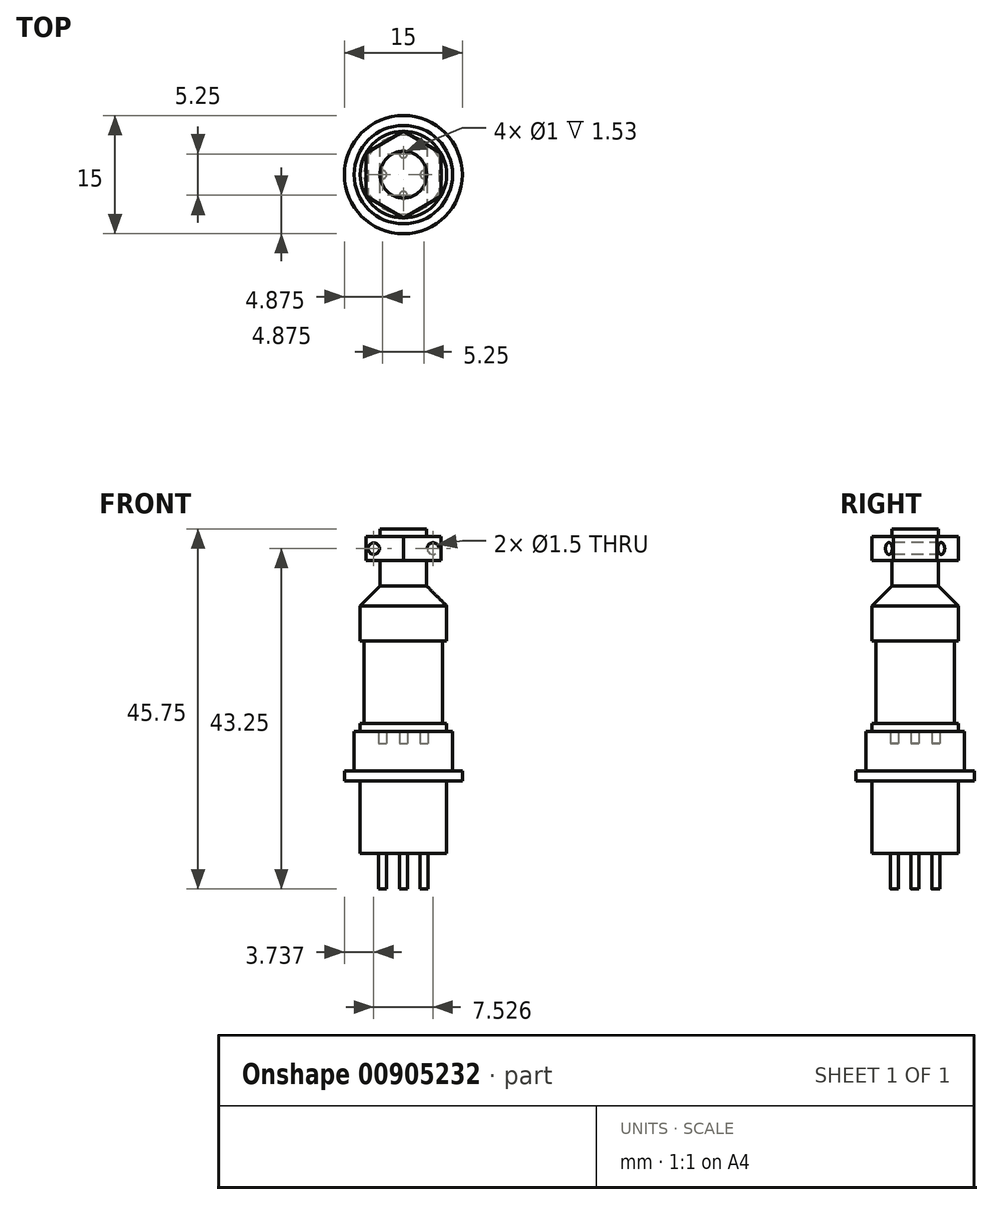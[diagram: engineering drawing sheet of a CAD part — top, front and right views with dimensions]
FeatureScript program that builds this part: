
annotation { "Feature Type Name" : "Feature", "Feature Type Description" : "" }
export const myFeature = defineFeature(function(context is Context, id is Id, definition is map)
    precondition{}
    {
        {
            var Q0;
            Q0=qCreatedBy(makeId("Top.planeOp"),FACE);
            var sketch = newSketch(context, id + "F0", { "sketchPlane" : qUnion([Q0])});
            skCircle(sketch, "E0", {"center": v(0, 0) * mm, "radius": 5.5 * mm});
            skSolve(sketch);
        }
        {
            var Q0;
            Q0 = qSketchRegion(id + "F0", true);
            extrude(context, id + "F1", {"entities" : qUnion([Q0]), "depth" : 9.25 * mm, "offsetDistance" : 25.4 * mm});
        }
        {
            var Q0;
            Q0=makeQuery(id+"F1.opExtrude","CAP_FACE",FACE,{"disambiguationData":[OSD([sQuery(id+"F0.wireOp",EDGE,"E0")])],"isStart":true});
            var sketch = newSketch(context, id + "F2", { "sketchPlane" : qUnion([Q0])});
            skLineSegment(sketch, "E1", {"start": v(0, 0) * mm, "end": v(0, 2.63) * mm});
            skCircle(sketch, "E2", {"center": v(0, 2.63) * mm, "radius": 0.5 * mm});
            skCircle(sketch, "E3.1.0", {"center": v(-2.63, 0) * mm, "radius": 0.5 * mm});
            skCircle(sketch, "E3.2.0", {"center": v(0, -2.63) * mm, "radius": 0.5 * mm});
            skCircle(sketch, "E3.3.0", {"center": v(2.63, 0) * mm, "radius": 0.5 * mm});
            skPoint(sketch, "E3.center", {"position": v(0, 0) * mm});
            skSolve(sketch);
        }
        {
            var Q0;
            Q0 = qSketchRegion(id + "F2", true);
            extrude(context, id + "F3", {"entities" : qUnion([Q0]), "operationType" : NewBodyOperationType.ADD, "depth" : 4.5 * mm, "offsetDistance" : 25.4 * mm, "hasSecondDirection" : true, "secondDirectionOppositeDirection" : true, "secondDirectionDepth" : 12.7 * mm});
        }
        {
            var Q0;
            Q0=makeQuery(id+"F1.opExtrude","CAP_FACE",FACE,{"disambiguationData":[OSD([sQuery(id+"F0.wireOp",EDGE,"E0")])],"isStart":false});
            var sketch = newSketch(context, id + "F4", { "sketchPlane" : qUnion([Q0])});
            skCircle(sketch, "E4", {"center": v(0, 0) * mm, "radius": 7.5 * mm});
            skSolve(sketch);
        }
        {
            var Q0;
            Q0 = qSketchRegion(id + "F4", true);
            extrude(context, id + "F5", {"entities" : qUnion([Q0]), "operationType" : NewBodyOperationType.ADD, "depth" : 1.25 * mm, "offsetDistance" : 25.4 * mm});
        }
        {
            var Q0;
            Q0=makeQuery(id+"F5.opExtrude","CAP_FACE",FACE,{"disambiguationData":[OSD([sQuery(id+"F4.wireOp",EDGE,"E4")])],"isStart":false});
            var sketch = newSketch(context, id + "F6", { "sketchPlane" : qUnion([Q0])});
            skCircle(sketch, "E5", {"center": v(0, 0) * mm, "radius": 6.25 * mm});
            skSolve(sketch);
        }
        {
            var Q0;
            Q0 = qSketchRegion(id + "F6", true);
            extrude(context, id + "F7", {"entities" : qUnion([Q0]), "operationType" : NewBodyOperationType.ADD, "depth" : 5 * mm, "offsetDistance" : 25.4 * mm});
        }
        {
            var Q0;
            Q0=makeQuery(id+"F7.opExtrude","CAP_FACE",FACE,{"disambiguationData":[OSD([sQuery(id+"F6.wireOp",EDGE,"E5")])],"isStart":false});
            var sketch = newSketch(context, id + "F8", { "sketchPlane" : qUnion([Q0])});
            skArc(sketch, "E6", {"start": v(2.58, 3.69) * mm, "mid": v(-3.19, -3.17) * mm, "end": v(3.7, 2.56) * mm});
            skArc(sketch, "E7", {"start": v(2.58, 3.69) * mm, "mid": v(2.89, 2.87) * mm, "end": v(3.7, 2.56) * mm});
            skSolve(sketch);
        }
        {
            var Q0;
            Q0 = qSketchRegion(id + "F8", true);
            extrude(context, id + "F9", {"entities" : qUnion([Q0]), "operationType" : NewBodyOperationType.REMOVE, "oppositeDirection" : true, "depth" : 9 * mm, "offsetDistance" : 25.4 * mm});
        }
        {
            var Q0;
            Q0 = qSketchRegion(id + "F2", true);
            extrude(context, id + "F10", {"entities" : qUnion([Q0]), "operationType" : NewBodyOperationType.ADD, "oppositeDirection" : true, "depth" : 13.97 * mm, "offsetDistance" : 25.4 * mm});
        }
        {
            var Q0;
            Q0=makeQuery(id+"F9.boolean.opBoolean","COPY",FACE,{"derivedFrom":makeQuery(id+"F9.opExtrude","CAP_FACE",FACE,{"disambiguationData":[OSD([sQuery(id+"F8.wireOp",EDGE,"E6"),sQuery(id+"F8.wireOp",EDGE,"E7")])],"isStart":false})});
            extrude(context, id + "F11", {"entities" : qUnion([Q0]), "depth" : 9 * mm, "offsetDistance" : 25.4 * mm});
        }
        {
            var Q0;
            Q0=makeQuery(id+"F11.opExtrude","CAP_FACE",FACE,{"disambiguationData":[OSD([sQuery(id+"F8.wireOp",EDGE,"E6"),sQuery(id+"F8.wireOp",EDGE,"E7")])],"isStart":false});
            var sketch = newSketch(context, id + "F12", { "sketchPlane" : qUnion([Q0])});
            skCircle(sketch, "E8", {"center": v(0, 0) * mm, "radius": 5.5 * mm});
            skSolve(sketch);
        }
        {
            var Q0;
            Q0 = qSketchRegion(id + "F12", true);
            extrude(context, id + "F13", {"entities" : qUnion([Q0]), "operationType" : NewBodyOperationType.ADD, "depth" : 1 * mm, "offsetDistance" : 25.4 * mm});
        }
        {
            var Q0;
            Q0=makeQuery(id+"F13.opExtrude","CAP_FACE",FACE,{"disambiguationData":[OSD([sQuery(id+"F12.wireOp",EDGE,"E8")])],"isStart":false});
            var sketch = newSketch(context, id + "F14", { "sketchPlane" : qUnion([Q0])});
            skCircle(sketch, "E9", {"center": v(0, 0) * mm, "radius": 5 * mm});
            skSolve(sketch);
        }
        {
            var Q0;
            Q0 = qSketchRegion(id + "F14", true);
            extrude(context, id + "F15", {"entities" : qUnion([Q0]), "operationType" : NewBodyOperationType.ADD, "depth" : 10.5 * mm, "offsetDistance" : 25.4 * mm});
        }
        {
            var Q0;
            Q0=makeQuery(id+"F15.opExtrude","CAP_FACE",FACE,{"disambiguationData":[OSD([sQuery(id+"F14.wireOp",EDGE,"E9")])],"isStart":false});
            var sketch = newSketch(context, id + "F16", { "sketchPlane" : qUnion([Q0])});
            skCircle(sketch, "E10", {"center": v(0, 0) * mm, "radius": 5.5 * mm});
            skSolve(sketch);
        }
        {
            var Q0;
            Q0 = qSketchRegion(id + "F16", true);
            extrude(context, id + "F17", {"entities" : qUnion([Q0]), "operationType" : NewBodyOperationType.ADD, "depth" : 7 * mm, "offsetDistance" : 25.4 * mm});
        }
        {
            var Q0;
            Q0=makeQuery(id+"F17.opExtrude","CAP_FACE",FACE,{"disambiguationData":[OSD([sQuery(id+"F16.wireOp",EDGE,"E10")])],"isStart":false});
            chamfer(context, id + "F18", {"entities" : qUnion([Q0]), "width" : 2.54 * mm, "tangentPropagation" : true});
        }
        {
            var Q0;
            Q0=makeQuery(id+"F17.opExtrude","CAP_FACE",FACE,{"disambiguationData":[OSD([sQuery(id+"F16.wireOp",EDGE,"E10")])],"isStart":false});
            extrude(context, id + "F19", {"entities" : qUnion([Q0]), "operationType" : NewBodyOperationType.ADD, "depth" : 7.25 * mm, "offsetDistance" : 25.4 * mm});
        }
        {
            var Q0;
            Q0=makeQuery(id+"F19.opExtrude","CAP_FACE",FACE,{"disambiguationData":[OSD([sQuery(id+"F16.wireOp",EDGE,"E10")])],"isStart":false});
            cPlane(context, id + "F20", {"entities" : qUnion([Q0]), "cplaneType" : CPlaneType.OFFSET, "offset" : 1 * mm, "oppositeDirection" : true, "width" : 152.4 * mm, "height" : 152.4 * mm});
        }
        {
            var Q0;
            Q0=qCreatedBy(id+"F20.planeOp",FACE);
            var sketch = newSketch(context, id + "F21", { "sketchPlane" : qUnion([Q0])});
            skCircle(sketch, "E11.cCircle", {"center": v(0, 0) * mm, "radius": 4.76 * mm, "construction": true});
            skLineSegment(sketch, "E11.0", {"start": v(4.76, -2.75) * mm, "end": v(0, -5.5) * mm});
            skLineSegment(sketch, "E11.1", {"start": v(0, -5.5) * mm, "end": v(-4.76, -2.75) * mm});
            skLineSegment(sketch, "E11.2", {"start": v(-4.76, -2.75) * mm, "end": v(-4.76, 2.75) * mm});
            skLineSegment(sketch, "E11.3", {"start": v(-4.76, 2.75) * mm, "end": v(0, 5.5) * mm});
            skLineSegment(sketch, "E11.4", {"start": v(0, 5.5) * mm, "end": v(4.76, 2.75) * mm});
            skLineSegment(sketch, "E11.5", {"start": v(4.76, 2.75) * mm, "end": v(4.76, -2.75) * mm});
            skPoint(sketch, "E11.0.midPoint", {"position": v(2.38, -4.13) * mm});
            skLineSegment(sketch, "E12", {"start": v(0, 0) * mm, "end": v(0, -5.5) * mm});
            skSolve(sketch);
        }
        {
            var Q0;
            Q0 = qSketchRegion(id + "F21", true);
            extrude(context, id + "F22", {"entities" : qUnion([Q0]), "operationType" : NewBodyOperationType.ADD, "oppositeDirection" : true, "depth" : 3 * mm, "offsetDistance" : 25.4 * mm});
        }
        {
            var Q0;
            Q0=qCreatedBy(makeId("Front.planeOp"),FACE);
            var sketch = newSketch(context, id + "F23", { "sketchPlane" : qUnion([Q0])});
            skLineSegment(sketch, "E13", {"start": v(0, 0) * mm, "end": v(0, 38.75) * mm});
            skLineSegment(sketch, "E14", {"start": v(0, 38.75) * mm, "end": v(-4.76, 38.75) * mm});
            skLineSegment(sketch, "E15", {"start": v(-4.76, 38.75) * mm, "end": v(-3.76, 38.75) * mm});
            skLineSegment(sketch, "E16.MirrorCS", {"start": v(4.76, 38.75) * mm, "end": v(3.76, 38.75) * mm});
            skLineSegment(sketch, "E17.MirrorCS", {"start": v(0, 38.75) * mm, "end": v(4.76, 38.75) * mm});
            skCircle(sketch, "E18", {"center": v(-3.76, 38.75) * mm, "radius": 0.75 * mm});
            skCircle(sketch, "E19.MirrorC", {"center": v(3.76, 38.75) * mm, "radius": 0.75 * mm});
            skSolve(sketch);
        }
        {
            var Q0;
            Q0 = qSketchRegion(id + "F23", true);
            extrude(context, id + "F24", {"entities" : qUnion([Q0]), "operationType" : NewBodyOperationType.REMOVE, "endBound" : BoundingType.SYMMETRIC, "oppositeDirection" : true, "depth" : 25.4 * mm, "offsetDistance" : 25.4 * mm});
        }
    });
